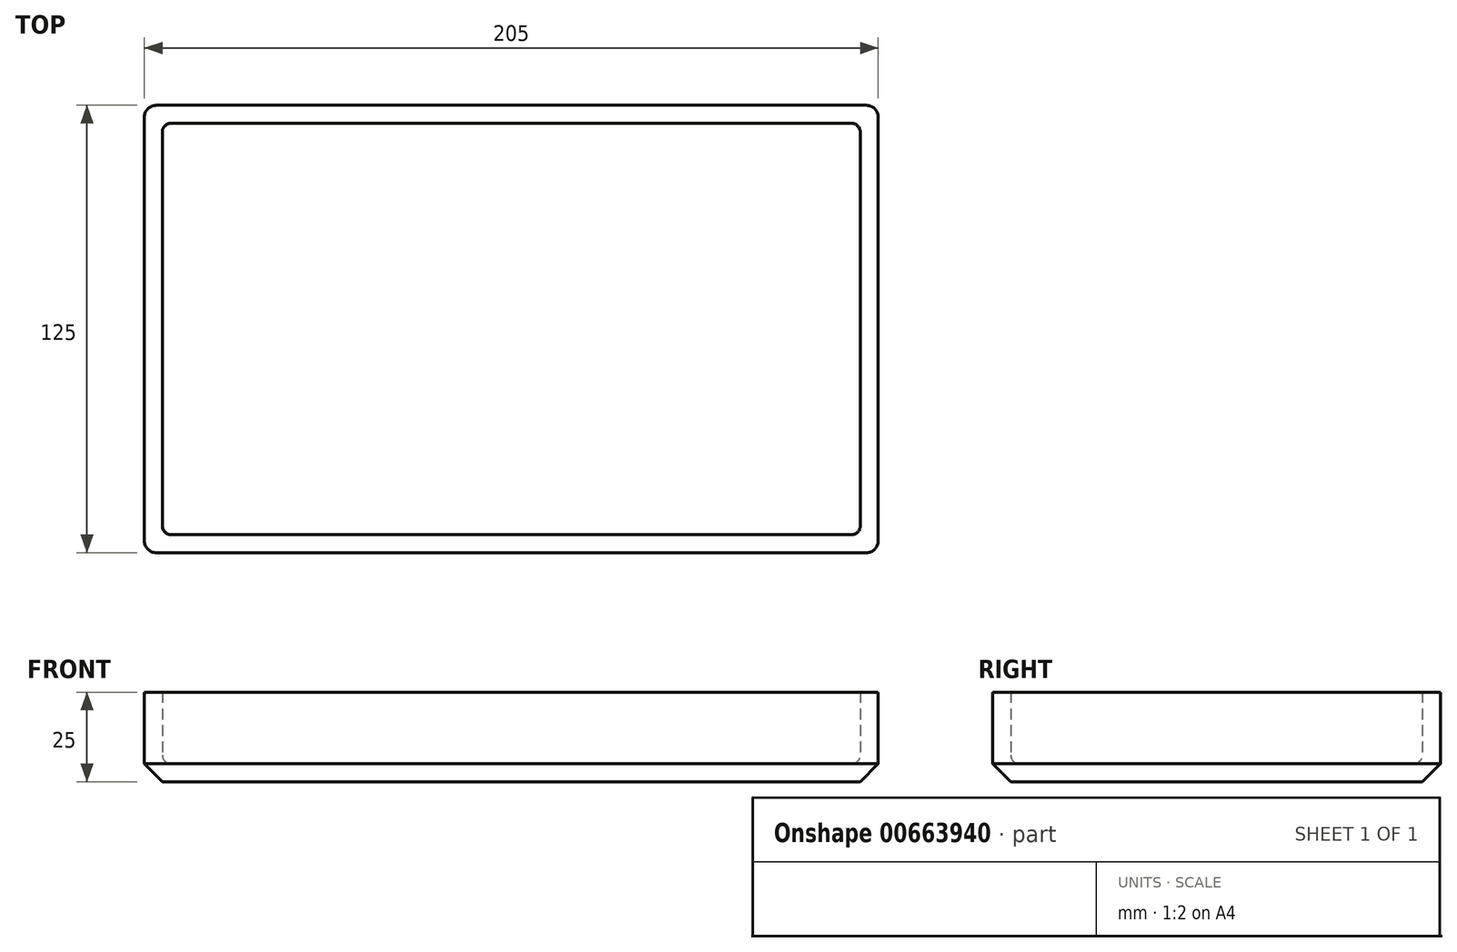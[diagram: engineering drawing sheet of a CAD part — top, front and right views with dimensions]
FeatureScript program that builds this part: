
annotation { "Feature Type Name" : "Feature", "Feature Type Description" : "" }
export const myFeature = defineFeature(function(context is Context, id is Id, definition is map)
    precondition{}
    {
        {
            assignVariable(context, id + "F0", {"name" : "wall_thickness", "anyValue" : 5});
        }
        {
            assignVariable(context, id + "F1", {"name" : "height", "anyValue" : 25});
        }
        {
            var Q0;
            Q0=qCreatedBy(makeId("Top.planeOp"),FACE);
            var sketch = newSketch(context, id + "F2", { "sketchPlane" : qUnion([Q0])});
            skLineSegment(sketch, "E0.bottom", {"start": v(102.5, 62.5) * mm, "end": v(-102.5, 62.5) * mm});
            skLineSegment(sketch, "E0.top", {"start": v(102.5, -62.5) * mm, "end": v(-102.5, -62.5) * mm});
            skLineSegment(sketch, "E0.left", {"start": v(102.5, 62.5) * mm, "end": v(102.5, -62.5) * mm});
            skLineSegment(sketch, "E0.right", {"start": v(-102.5, 62.5) * mm, "end": v(-102.5, -62.5) * mm});
            skPoint(sketch, "E0.middle", {"position": v(0, 0) * mm});
            skSolve(sketch);
        }
        {
            var Q0;
            Q0=makeQuery(id+"F2.imprint","IMPRINT",FACE,{"disambiguationData":[TD([[makeQuery(id+"F2.imprint","IMPRINT",EDGE,{"derivedFrom":sQuery(id+"F2.wireOp",EDGE,"E0.bottom")}),1.0]])]});
            extrude(context, id + "F3", {"entities" : qUnion([Q0]), "depth" : (getVariable(context, 'height')) * mm, "offsetDistance" : 25 * mm});
        }
        {
            var Q0;
            Q0=makeQuery(id+"F3.opExtrude","CAP_FACE",FACE,{"disambiguationData":[OSD([sQuery(id+"F2.wireOp",EDGE,"E0.bottom"),sQuery(id+"F2.wireOp",EDGE,"E0.top"),sQuery(id+"F2.wireOp",EDGE,"E0.left"),sQuery(id+"F2.wireOp",EDGE,"E0.right")])],"isStart":false});
            shell(context, id + "F4", {"entities" : qUnion([Q0]), "thickness" : (getVariable(context, 'wall_thickness')) * mm});
        }
        {
            var Q0;
            Q0=makeQuery(id+"F3.opExtrude","CAP_EDGE",EDGE,{"disambiguationData":[OSD([sQuery(id+"F2.wireOp",EDGE,"E0.bottom")])],"isStart":true});
            var Q1;
            Q1=makeQuery(id+"F3.opExtrude","CAP_EDGE",EDGE,{"disambiguationData":[OSD([sQuery(id+"F2.wireOp",EDGE,"E0.right")])],"isStart":true});
            var Q2;
            Q2=makeQuery(id+"F3.opExtrude","CAP_EDGE",EDGE,{"disambiguationData":[OSD([sQuery(id+"F2.wireOp",EDGE,"E0.top")])],"isStart":true});
            var Q3;
            Q3=makeQuery(id+"F3.opExtrude","CAP_EDGE",EDGE,{"disambiguationData":[OSD([sQuery(id+"F2.wireOp",EDGE,"E0.left")])],"isStart":true});
            chamfer(context, id + "F5", {"entities" : qUnion([Q0, Q1, Q2, Q3]), "width" : (getVariable(context, 'wall_thickness')) * mm, "tangentPropagation" : true});
        }
        {
            var Q0;
            Q0=makeQuery(id+"F5.opChamfer","BLEND_EDGE",EDGE,{"blendedFrom":[makeQuery(id+"F3.opExtrude","CAP_EDGE",EDGE,{"disambiguationData":[OSD([sQuery(id+"F2.wireOp",EDGE,"E0.top")])],"isStart":true}),makeQuery(id+"F3.opExtrude","CAP_EDGE",EDGE,{"disambiguationData":[OSD([sQuery(id+"F2.wireOp",EDGE,"E0.left")])],"isStart":true})],"blendedInto":[]});
            var Q1;
            Q1=makeQuery(id+"F5.opChamfer","BLEND_EDGE",EDGE,{"blendedFrom":[makeQuery(id+"F3.opExtrude","CAP_EDGE",EDGE,{"disambiguationData":[OSD([sQuery(id+"F2.wireOp",EDGE,"E0.bottom")])],"isStart":true}),makeQuery(id+"F3.opExtrude","CAP_EDGE",EDGE,{"disambiguationData":[OSD([sQuery(id+"F2.wireOp",EDGE,"E0.right")])],"isStart":true})],"blendedInto":[]});
            var Q2;
            Q2=makeQuery(id+"F5.opChamfer","BLEND_EDGE",EDGE,{"blendedFrom":[makeQuery(id+"F3.opExtrude","CAP_EDGE",EDGE,{"disambiguationData":[OSD([sQuery(id+"F2.wireOp",EDGE,"E0.top")])],"isStart":true}),makeQuery(id+"F3.opExtrude","CAP_EDGE",EDGE,{"disambiguationData":[OSD([sQuery(id+"F2.wireOp",EDGE,"E0.right")])],"isStart":true})],"blendedInto":[]});
            var Q3;
            Q3=makeQuery(id+"F5.opChamfer","BLEND_EDGE",EDGE,{"blendedFrom":[makeQuery(id+"F3.opExtrude","CAP_EDGE",EDGE,{"disambiguationData":[OSD([sQuery(id+"F2.wireOp",EDGE,"E0.bottom")])],"isStart":true}),makeQuery(id+"F3.opExtrude","CAP_EDGE",EDGE,{"disambiguationData":[OSD([sQuery(id+"F2.wireOp",EDGE,"E0.left")])],"isStart":true})],"blendedInto":[]});
            fillet(context, id + "F6", {"entities" : qUnion([Q0, Q1, Q2, Q3]), "radius" : 5 * mm, "tangentPropagation" : true, "allowEdgeOverflow" : false});
        }
        {
            var Q0;
            Q0=makeQuery(id+"F4.opShell","OFFSET_EDGE",EDGE,{"disambiguationData":[OSD([sQuery(id+"F2.wireOp",EDGE,"E0.top"),sQuery(id+"F2.wireOp",EDGE,"E0.right")])]});
            var Q1;
            Q1=makeQuery(id+"F4.opShell","OFFSET_EDGE",EDGE,{"disambiguationData":[OSD([sQuery(id+"F2.wireOp",EDGE,"E0.bottom"),sQuery(id+"F2.wireOp",EDGE,"E0.right")])]});
            var Q2;
            Q2=makeQuery(id+"F4.opShell","OFFSET_EDGE",EDGE,{"disambiguationData":[OSD([sQuery(id+"F2.wireOp",EDGE,"E0.bottom"),sQuery(id+"F2.wireOp",EDGE,"E0.left")])]});
            var Q3;
            Q3=makeQuery(id+"F4.opShell","OFFSET_EDGE",EDGE,{"disambiguationData":[OSD([sQuery(id+"F2.wireOp",EDGE,"E0.top"),sQuery(id+"F2.wireOp",EDGE,"E0.left")])]});
            var Q4;
            {var subQ0=sQuery(id+"F2.wireOp",EDGE,"E0.top");Q4=makeQuery(id+"F4.opShell","OFFSET_EDGE",EDGE,{"disambiguationData":[OSD([subQ0]),TDD([makeQuery(id+"F3.opExtrude","CAP_EDGE",EDGE,{"disambiguationData":[OSD([subQ0])],"isStart":true})])]});}
            var Q5;
            {var subQ0=sQuery(id+"F2.wireOp",EDGE,"E0.left");Q5=makeQuery(id+"F4.opShell","OFFSET_EDGE",EDGE,{"disambiguationData":[OSD([subQ0]),TDD([makeQuery(id+"F3.opExtrude","CAP_EDGE",EDGE,{"disambiguationData":[OSD([subQ0])],"isStart":true})])]});}
            var Q6;
            {var subQ0=sQuery(id+"F2.wireOp",EDGE,"E0.bottom");Q6=makeQuery(id+"F4.opShell","OFFSET_EDGE",EDGE,{"disambiguationData":[OSD([subQ0]),TDD([makeQuery(id+"F3.opExtrude","CAP_EDGE",EDGE,{"disambiguationData":[OSD([subQ0])],"isStart":true})])]});}
            var Q7;
            {var subQ0=sQuery(id+"F2.wireOp",EDGE,"E0.right");Q7=makeQuery(id+"F4.opShell","OFFSET_EDGE",EDGE,{"disambiguationData":[OSD([subQ0]),TDD([makeQuery(id+"F3.opExtrude","CAP_EDGE",EDGE,{"disambiguationData":[OSD([subQ0])],"isStart":true})])]});}
            fillet(context, id + "F7", {"entities" : qUnion([Q0, Q1, Q2, Q3, Q4, Q5, Q6, Q7]), "radius" : (getVariable(context, 'wall_thickness') / 2) * mm, "tangentPropagation" : true, "allowEdgeOverflow" : false});
        }
        {
            var Q0;
            Q0=makeQuery(id+"F3.opExtrude","SWEPT_EDGE",EDGE,{"disambiguationData":[OSD([sQuery(id+"F2.wireOp",EDGE,"E0.bottom"),sQuery(id+"F2.wireOp",EDGE,"E0.left")])]});
            var Q1;
            Q1=makeQuery(id+"F3.opExtrude","SWEPT_EDGE",EDGE,{"disambiguationData":[OSD([sQuery(id+"F2.wireOp",EDGE,"E0.top"),sQuery(id+"F2.wireOp",EDGE,"E0.left")])]});
            var Q2;
            Q2=makeQuery(id+"F3.opExtrude","SWEPT_EDGE",EDGE,{"disambiguationData":[OSD([sQuery(id+"F2.wireOp",EDGE,"E0.top"),sQuery(id+"F2.wireOp",EDGE,"E0.right")])]});
            var Q3;
            Q3=makeQuery(id+"F3.opExtrude","SWEPT_EDGE",EDGE,{"disambiguationData":[OSD([sQuery(id+"F2.wireOp",EDGE,"E0.bottom"),sQuery(id+"F2.wireOp",EDGE,"E0.right")])]});
            fillet(context, id + "F8", {"entities" : qUnion([Q0, Q1, Q2, Q3]), "radius" : (getVariable(context, 'wall_thickness') * .66) * mm, "tangentPropagation" : true, "allowEdgeOverflow" : false});
        }
    });
